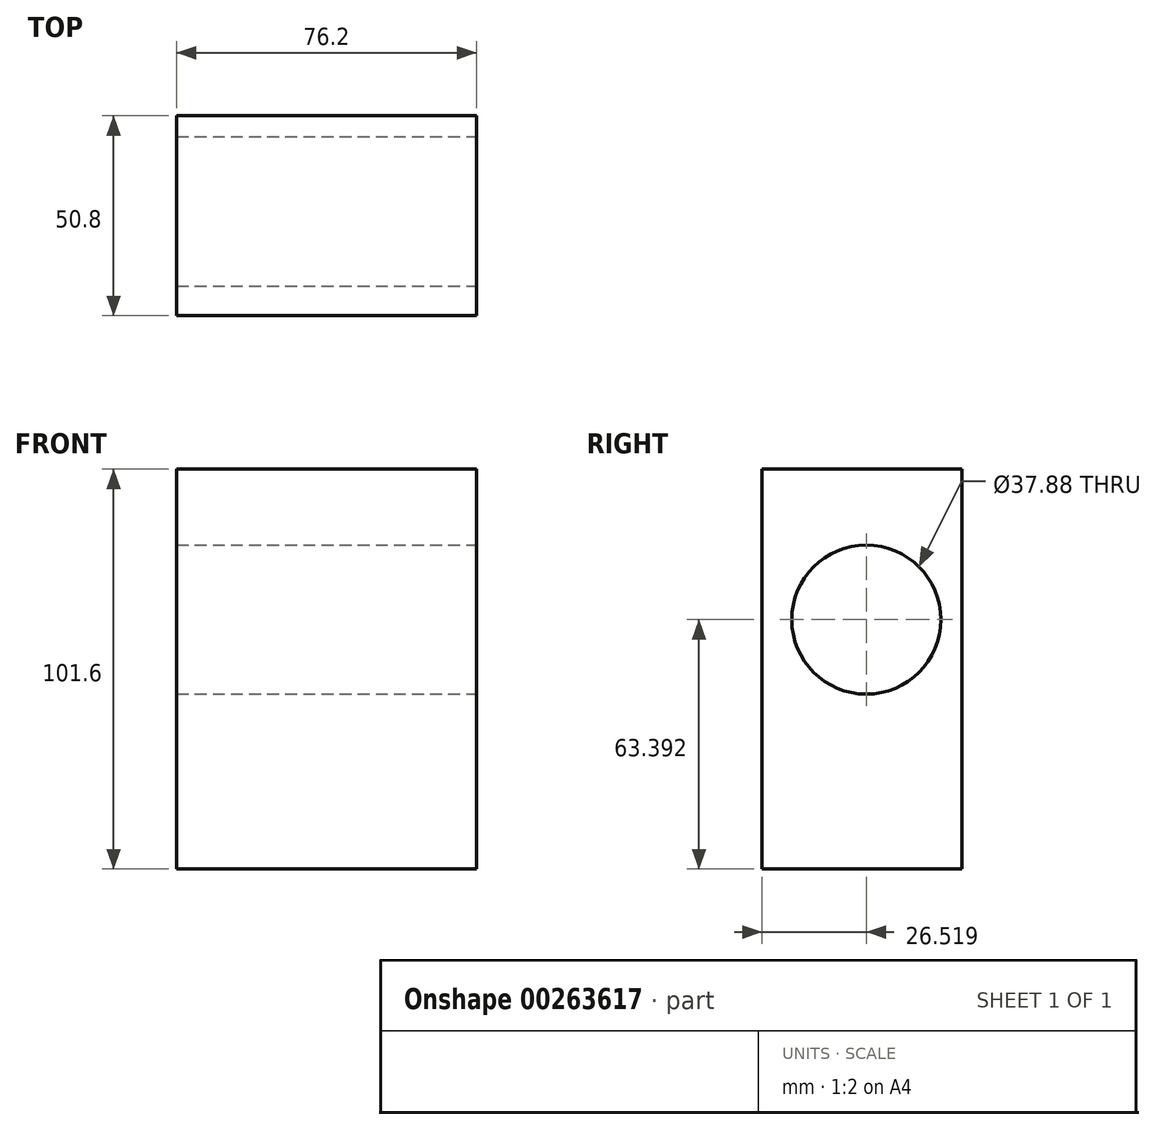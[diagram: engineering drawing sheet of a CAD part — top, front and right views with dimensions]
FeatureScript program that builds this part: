
annotation { "Feature Type Name" : "Feature", "Feature Type Description" : "" }
export const myFeature = defineFeature(function(context is Context, id is Id, definition is map)
    precondition{}
    {
        {
            var Q0;
            Q0=qCreatedBy(makeId("Front.planeOp"),FACE);
            var sketch = newSketch(context, id + "F0", { "sketchPlane" : qUnion([Q0])});
            skLineSegment(sketch, "E0.bottom", {"start": v(0, 0) * mm, "end": v(76.2, 0) * mm});
            skLineSegment(sketch, "E0.top", {"start": v(0, 101.6) * mm, "end": v(76.2, 101.6) * mm});
            skLineSegment(sketch, "E0.left", {"start": v(0, 0) * mm, "end": v(0, 101.6) * mm});
            skLineSegment(sketch, "E0.right", {"start": v(76.2, 0) * mm, "end": v(76.2, 101.6) * mm});
            skSolve(sketch);
        }
        {
            var Q0;
            Q0=makeQuery(id+"F0.imprint","IMPRINT",FACE,{"disambiguationData":[TD([[makeQuery(id+"F0.imprint","IMPRINT",EDGE,{"derivedFrom":sQuery(id+"F0.wireOp",EDGE,"E0.bottom")}),1.0]])]});
            extrude(context, id + "F1", {"entities" : qUnion([Q0]), "oppositeDirection" : true, "depth" : 50.8 * mm});
        }
        {
            var Q0;
            Q0=makeQuery(id+"F1.opExtrude","SWEPT_FACE",FACE,{"disambiguationData":[OSD([sQuery(id+"F0.wireOp",EDGE,"E0.right")])]});
            var sketch = newSketch(context, id + "F2", { "sketchPlane" : qUnion([Q0])});
            skCircle(sketch, "E1", {"center": v(26.52, 63.4) * mm, "radius": 18.94 * mm});
            skSolve(sketch);
        }
        {
            var Q0;
            Q0=makeQuery(id+"F2.imprint","IMPRINT",FACE,{"disambiguationData":[TD([[makeQuery(id+"F2.imprint","IMPRINT",EDGE,{"derivedFrom":sQuery(id+"F2.wireOp",EDGE,"E1")}),1.0]])]});
            extrude(context, id + "F3", {"entities" : qUnion([Q0]), "operationType" : NewBodyOperationType.REMOVE, "endBound" : BoundingType.UP_TO_NEXT, "oppositeDirection" : true, "depth" : 25.4 * mm});
        }
    });
